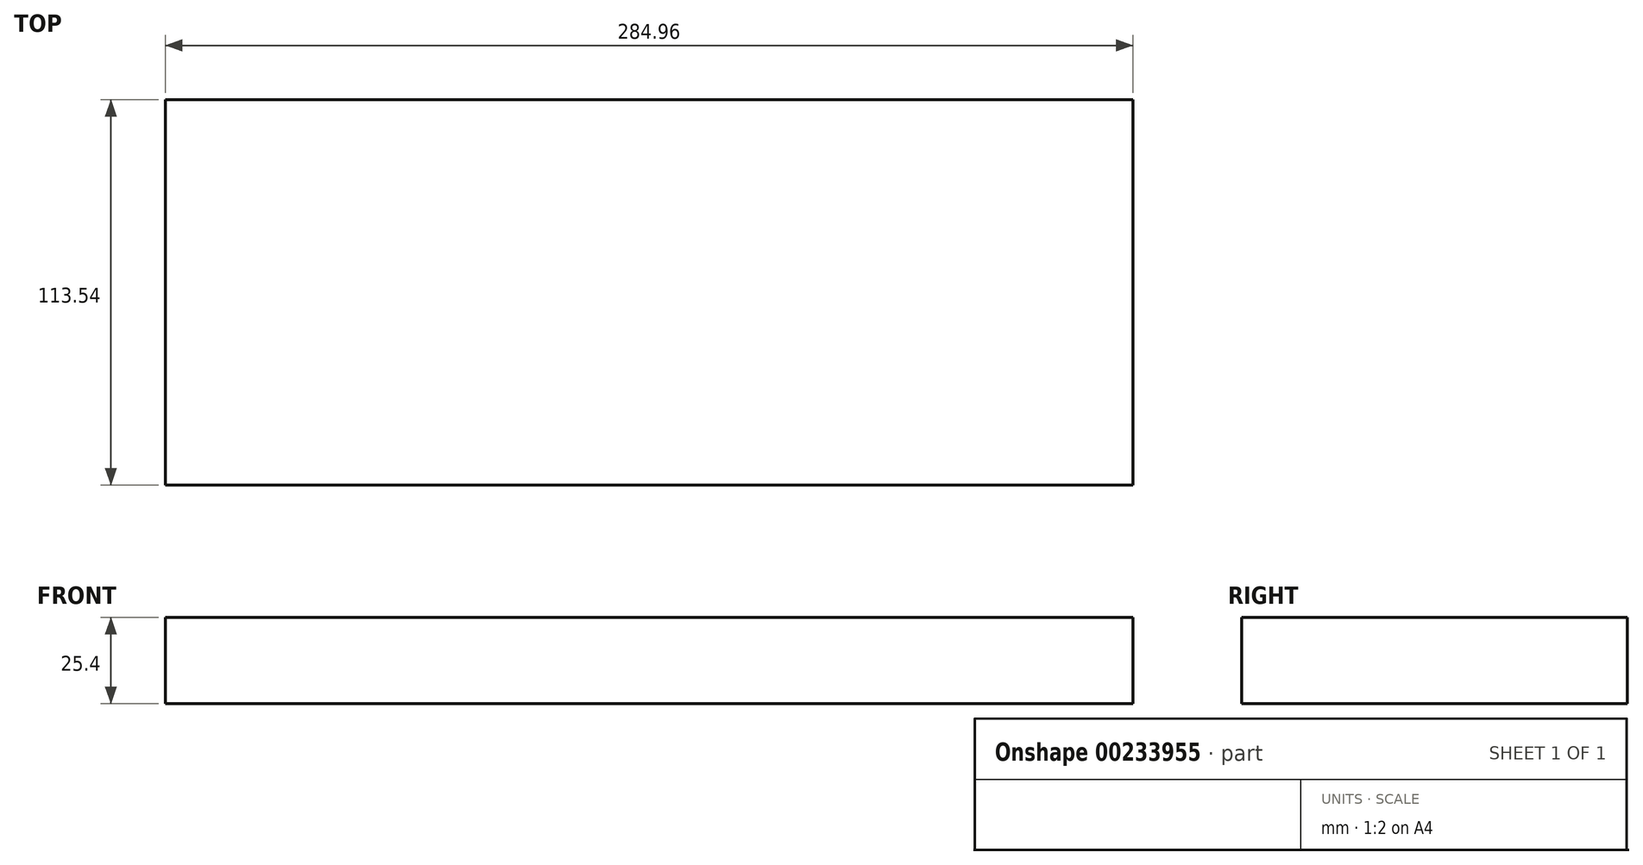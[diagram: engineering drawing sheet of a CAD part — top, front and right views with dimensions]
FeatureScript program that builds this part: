
annotation { "Feature Type Name" : "Feature", "Feature Type Description" : "" }
export const myFeature = defineFeature(function(context is Context, id is Id, definition is map)
    precondition{}
    {
        {
            var Q0;
            Q0=qCreatedBy(makeId("Top.planeOp"),FACE);
            var sketch = newSketch(context, id + "F0", { "sketchPlane" : qUnion([Q0])});
            skLineSegment(sketch, "E0.bottom", {"start": v(-152.25, 63.93) * mm, "end": v(132.7, 63.93) * mm});
            skLineSegment(sketch, "E0.top", {"start": v(-152.25, -49.6) * mm, "end": v(132.7, -49.6) * mm});
            skLineSegment(sketch, "E0.left", {"start": v(-152.25, 63.93) * mm, "end": v(-152.25, -49.6) * mm});
            skLineSegment(sketch, "E0.right", {"start": v(132.7, 63.93) * mm, "end": v(132.7, -49.6) * mm});
            skSolve(sketch);
        }
        {
            var Q0;
            Q0 = qSketchRegion(id + "F0", true);
            extrude(context, id + "F1", {"entities" : qUnion([Q0]), "depth" : 25.4 * mm});
        }
    });
